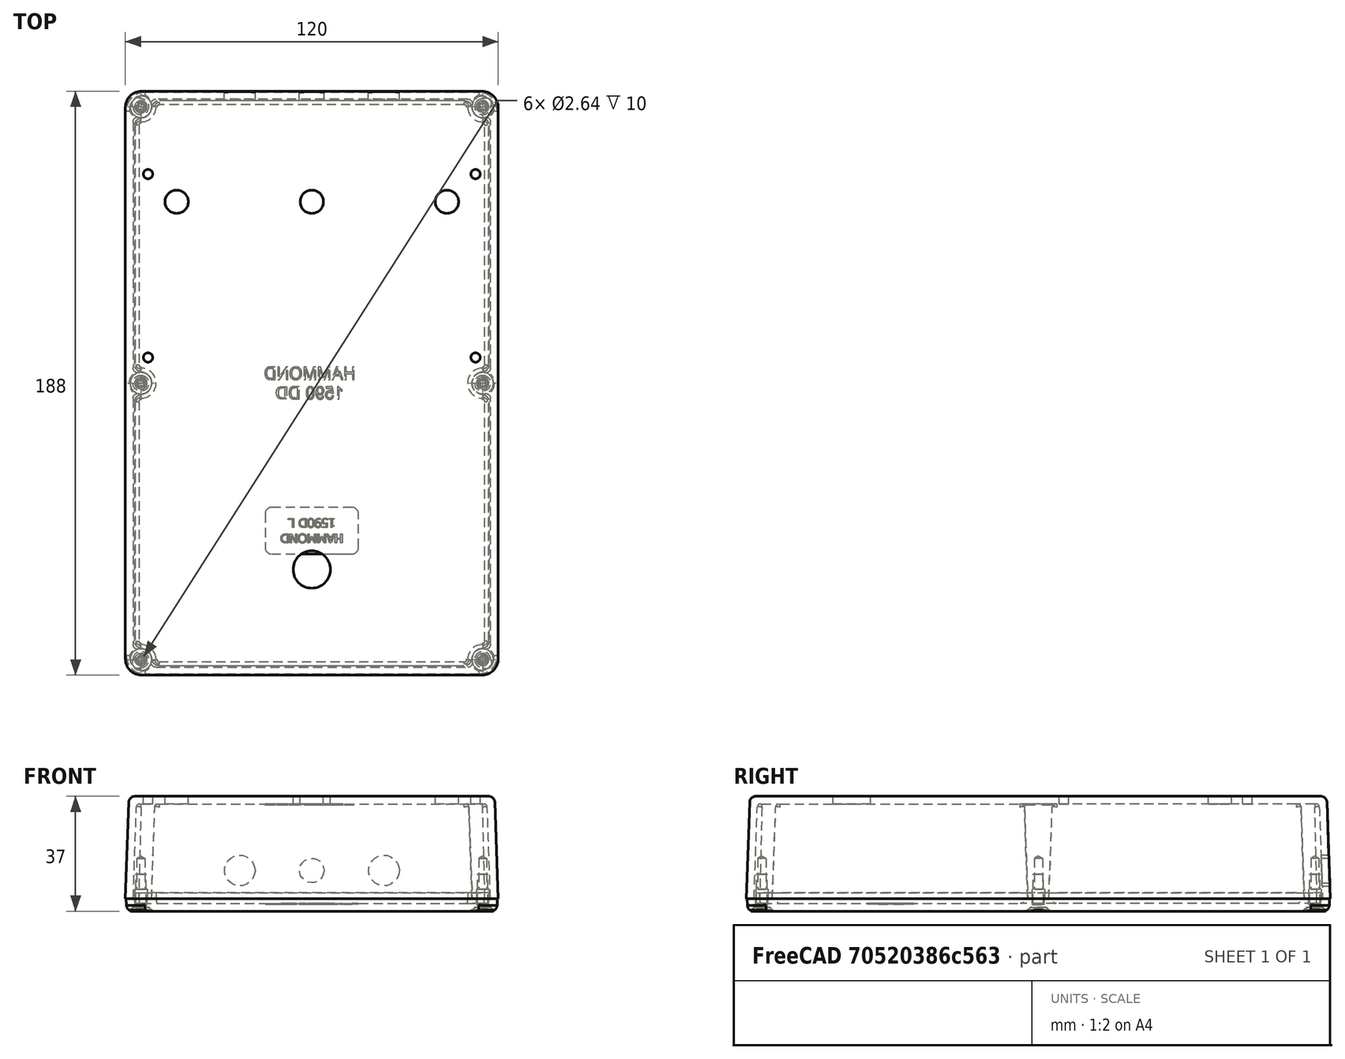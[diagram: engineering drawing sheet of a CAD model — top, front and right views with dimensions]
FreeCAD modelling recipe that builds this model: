
FCSTD DOCUMENT  (FreeCAD 0.19R18750 (Git))
Label: #700-000-A - Enclosure [1590DD, Portrait]
License: All rights reserved
LicenseURL: http://en.wikipedia.org/wiki/All_rights_reserved
objects: Part::Cylinder×11, PartDesign::ShapeBinder×9, Part::Feature×8, PartDesign::Plane×5, App::Part×4, Part::MultiFuse×2, PartDesign::Body×1, Part::Cut×1
note: 37 computed .brp shape members not serialized (recipe doc carries the construction recipe); baked Part::Feature solids carry a one-line shape summary decoded from their .brp

FEATURE [PartDesign::Plane] DatumPlane  label="Origin_XY_DatumPlane"
  AttachmentOffset = pos=(-75,-100,0) rot=(0,0,1;0rad)
  Length = 122.361
  MapMode = 5
  Placement = pos=(-75,-100,0) rot=(0,0,1;0rad)
  ResizeMode = 1
  Support = -> [XY_Plane001]
  Width = 200
FEATURE [Part::Feature] Part__Feature  label="#700-001 - 1590DD Box"
  Placement = pos=(0,0,0) rot=(0.707107,0.707107,0;3.14159rad)
  shape: bbox 120 x 188 x 451.1 mm, 273 faces (baked)
FEATURE [Part::Feature] Part__Feature001  label="#700-001 - 1590DD - Lid"
  Placement = pos=(0,0,0) rot=(0,0.707107,0.707107;3.14159rad)
  shape: bbox 187.5 x 5.937 x 119.5 mm, 345 faces (baked)
FEATURE [Part::Feature] Part__Feature002  label="#700-001 - 1590DD - Screw 4/6"
  Placement = pos=(1.2e-14,1.5362,-55) rot=(0,1,0;0.650238rad)
  shape: bbox 6.871 x 11.85 x 6.871 mm, 25 faces (baked)
FEATURE [Part::Feature] Part__Feature003  label="#700-001 - 1590DD - Screw 2/6"
  Placement = pos=(-1.2e-14,1.5362,55) rot=(0,1,0;0.650238rad)
  shape: bbox 6.871 x 11.85 x 6.871 mm, 25 faces (baked)
FEATURE [Part::Feature] Part__Feature004  label="#700-001 - 1590DD - Screw 1/6"
  Placement = pos=(-89,1.5362,55) rot=(0,1,0;0.650238rad)
  shape: bbox 6.871 x 11.85 x 6.871 mm, 25 faces (baked)
FEATURE [Part::Feature] Part__Feature005  label="#700-001 - 1590DD - Screw 3/6"
  Placement = pos=(-89,1.5362,-55) rot=(0,-1,0;0.529817rad)
  shape: bbox 6.871 x 11.85 x 6.871 mm, 25 faces (baked)
FEATURE [Part::Feature] Part__Feature006  label="#700-001 - 1590DD - Screw 5/6"
  Placement = pos=(89,1.5362,55) rot=(0,0,1;0rad)
  shape: bbox 6.871 x 11.85 x 6.871 mm, 25 faces (baked)
FEATURE [Part::Feature] Part__Feature007  label="#700-001 - 1590DD - Screw 6/6"
  Placement = pos=(89,1.5362,-55) rot=(0,0,1;0rad)
  shape: bbox 6.871 x 11.85 x 6.871 mm, 25 faces (baked)
FEATURE [Part::MultiFuse] Fusion  label="#700-000 - Enclosure - Lid & Screws, Fusion"
  Placement = pos=(0,0,0) rot=(0.57735,-0.57735,0.57735;4.18879rad)
  Shapes = -> [Part__Feature001,Part__Feature004,Part__Feature003,Part__Feature005,Part__Feature002,Part__Feature006,Part__Feature007]
FEATURE [Part::Cylinder] Cylinder  label="Drill - Potentiometer - Rate [D=7.5, X=-43.5, Y=58.42]"
  Angle = 360
  AttacherType = Attacher::AttachEngine3D
  Height = 10
  Placement = pos=(-43.498,58.42,25) rot=(0,0,1;0rad)
  Radius = 3.75
FEATURE [Part::Cylinder] Cylinder001  label="Drill - Potentiometer - Depth [D7.5, X=0.0, Y = 58.42]]"
  Angle = 360
  AttacherType = Attacher::AttachEngine3D
  Height = 10
  Placement = pos=(0,58.42,25) rot=(0,0,1;0rad)
  Radius = 3.75
FEATURE [Part::Cylinder] Cylinder002  label="Drill - Potentiometer - Feedback [D=7.5, X=43.5, Y=58.42]"
  Angle = 360
  AttacherType = Attacher::AttachEngine3D
  Height = 10
  Placement = pos=(43.498,58.42,25) rot=(0,0,1;0rad)
  Radius = 3.75
FEATURE [PartDesign::Plane] DatumPlane001  label="Enclosure_Face_XY_DatumPlane"
  Length = 60
  MapMode = 5
  Placement = pos=(0,0,30.5) rot=(1,0,0;3.14159rad)
  ResizeMode = 0
  Width = 60
FEATURE [Part::Cylinder] Cylinder003  label="Drill - Standoff 4/4 [D=3.0, X=-52.705, Y=8.26]"
  Angle = 360
  AttacherType = Attacher::AttachEngine3D
  Height = 10
  Placement = pos=(-52.705,8.26,26) rot=(0,0,1;0rad)
  Radius = 1.5
FEATURE [Part::Cylinder] Cylinder004  label="Drill - Standoff 3/4 [D=3.0, X=52.705, Y=8.26]"
  Angle = 360
  AttacherType = Attacher::AttachEngine3D
  Height = 10
  Placement = pos=(52.705,8.26,26) rot=(0,0,1;0rad)
  Radius = 1.5
FEATURE [Part::Cylinder] Cylinder005  label="Drill - Standoff 2/4 [D=3.0, X=-52.705, Y=67.31]"
  Angle = 360
  AttacherType = Attacher::AttachEngine3D
  Height = 10
  Placement = pos=(-52.705,67.31,26) rot=(0,0,1;0rad)
  Radius = 1.5
FEATURE [Part::Cylinder] Cylinder006  label="Drill - Standoff 1/4 [D=3.0, X=52.705, Y=67.31]"
  Angle = 360
  AttacherType = Attacher::AttachEngine3D
  Height = 10
  Placement = pos=(52.705,67.31,26) rot=(0,0,1;0rad)
  Radius = 1.5
FEATURE [App::Part] Part001  label="#700-000 - Enclosure - Lid & Screws"
  Group = -> [Part__Feature004,Part__Feature007,Part__Feature005,Part__Feature001,Part__Feature003,Part__Feature006,Part__Feature002,Fusion]
  Origin = -> Origin002
  Placement = pos=(0,0,0) rot=(0,0,1;3.14159rad)
FEATURE [PartDesign::ShapeBinder] ShapeBinder  label="Enclosure_Lid_Inside"
  Placement = pos=(0,0,0) rot=(0.707107,0.707107,0;3.14159rad)
  Support = -> [Fusion]
  TraceSupport = false
FEATURE [PartDesign::ShapeBinder] ShapeBinder001  label="Enclosure_Lid_Lip"
  Placement = pos=(0,0,0) rot=(0.707107,0.707107,0;3.14159rad)
  Support = -> [Fusion]
  TraceSupport = false
FEATURE [PartDesign::ShapeBinder] ShapeBinder002  label="Enclosure_Lid_Outside"
  Placement = pos=(0,0,0) rot=(0.707107,0.707107,0;3.14159rad)
  Support = -> [Fusion]
  TraceSupport = false
FEATURE [PartDesign::ShapeBinder] ShapeBinder003  label="Enclosure_Box_Top_Outside"
  Placement = pos=(0,0,0) rot=(0.707107,0.707107,0;3.14159rad)
  Support = -> [Part__Feature]
  TraceSupport = false
FEATURE [PartDesign::ShapeBinder] ShapeBinder004  label="Enclosure_Box_Top_Inside"
  Placement = pos=(0,0,0) rot=(0.707107,0.707107,0;3.14159rad)
  Support = -> [Part__Feature]
  TraceSupport = false
FEATURE [PartDesign::ShapeBinder] ShapeBinder005  label="Enclosure_Box_Rear_Outside"
  Placement = pos=(0,0,0) rot=(0.707107,0.707107,0;3.14159rad)
  Support = -> [Part__Feature]
  TraceSupport = false
FEATURE [PartDesign::ShapeBinder] ShapeBinder006  label="Enclosure_Box_Rear_Inside"
  Placement = pos=(0,0,0) rot=(0.707107,0.707107,0;3.14159rad)
  Support = -> [Part__Feature]
  TraceSupport = false
FEATURE [PartDesign::ShapeBinder] ShapeBinder007  label="Enclosure_Box_Front_Outside"
  Placement = pos=(0,0,0) rot=(0.707107,0.707107,0;3.14159rad)
  Support = -> [Part__Feature]
  TraceSupport = false
FEATURE [PartDesign::ShapeBinder] ShapeBinder008  label="Enclosure_Box_Front_Inside"
  Placement = pos=(0,0,0) rot=(0.707107,0.707107,0;3.14159rad)
  Support = -> [Part__Feature]
  TraceSupport = false
FEATURE [Part::Cylinder] Cylinder007  label="Drill - Audio Jack 1/2 [D=10.0, X=-23.2, Z=9.1]"
  Angle = 360
  AttacherType = Attacher::AttachEngine3D
  Height = 10
  Placement = pos=(-23.2,90,9.1) rot=(-1,0,0;1.5708rad)
  Radius = 5
  expr: .Placement.Base.z = 1 + 1.6000000000000001 + 6.5
FEATURE [Part::Cylinder] Cylinder008  label="Drill - Audio Jack 2/2 [D=10.0, X=23.2, Z=9.1]"
  Angle = 360
  AttacherType = Attacher::AttachEngine3D
  Height = 10
  Placement = pos=(23.2,90,9.1) rot=(-1,0,0;1.5708rad)
  Radius = 5
  expr: .Placement.Base.z = 1 + 1.6000000000000001 + 6.5
FEATURE [Part::Cylinder] Cylinder009  label="Drill - Power Jack [D=8.0, X=0.0, Y=9.1]"
  Angle = 360
  AttacherType = Attacher::AttachEngine3D
  Height = 10
  Placement = pos=(0,90,9.1) rot=(-1,0,0;1.5708rad)
  Radius = 4
FEATURE [PartDesign::Plane] DatumPlane002  label="DatumPlane_Rear_Inside"
  Length = 60.17
  MapMode = 5
  Placement = pos=(2.03e-14,91.387,3.19131) rot=(0,0.71934,-0.694658;3.14159rad)
  ResizeMode = 0
  Support = -> [ShapeBinder006]
  Width = 61.8845
FEATURE [PartDesign::Plane] DatumPlane003  label="DatumPlane_Top_Inside"
  Length = 60
  MapMode = 5
  Placement = pos=(0,0,30.5) rot=(0.707107,0.707107,0;3.14159rad)
  ResizeMode = 0
  Support = -> [ShapeBinder004]
  Width = 60
FEATURE [PartDesign::Plane] DatumPlane004  label="DatumPlane_Lid_Inside"
  Length = 60
  MapMode = 5
  Placement = pos=(0,0,-1.5) rot=(0,0,1;1.5708rad)
  ResizeMode = 0
  Support = -> [ShapeBinder]
  Width = 60
FEATURE [PartDesign::Body] Body  label="Datum References"
  Group = -> [DatumPlane,DatumPlane001,ShapeBinder,ShapeBinder001,ShapeBinder002,ShapeBinder003,ShapeBinder004,ShapeBinder005,ShapeBinder006,ShapeBinder007,ShapeBinder008,DatumPlane002,DatumPlane003,DatumPlane004]
  Origin = -> Origin001
FEATURE [App::Part] Part003  label="#700-000 - Datum References"
  Group = -> [Body]
  Origin = -> Origin004
FEATURE [Part::Cylinder] Cylinder010  label="Drill - Footswitch [D=12.0, X=0.0, Y=-60.0]"
  Angle = 360
  AttacherType = Attacher::AttachEngine3D
  Height = 10
  Placement = pos=(0,-60,25) rot=(0,0,1;0rad)
  Radius = 6
FEATURE [Part::MultiFuse] Fusion001  label="Drills"
  Shapes = -> [Cylinder,Cylinder002,Cylinder001,Cylinder003,Cylinder004,Cylinder005,Cylinder006,Cylinder007,Cylinder008,Cylinder009,Cylinder010]
FEATURE [Part::Cut] Cut  label="#700-000 - Enclosure - Box, Drilled"
  Base = -> Part__Feature
  Tool = -> Fusion001
FEATURE [App::Part] Part002  label="#700-000 - Enclosure - Box, Machined"
  Group = -> [Part__Feature,Fusion001,Cylinder002,Cylinder006,Cylinder004,Cylinder005,Cylinder,Cylinder001,Cylinder003,Cut]
  Origin = -> Origin003
FEATURE [App::Part] Part  label="#700-000-A - Enclosure [1590DD, Portrait]"
  Group = -> [Part001,Part002,Part003]
  Origin = -> Origin
